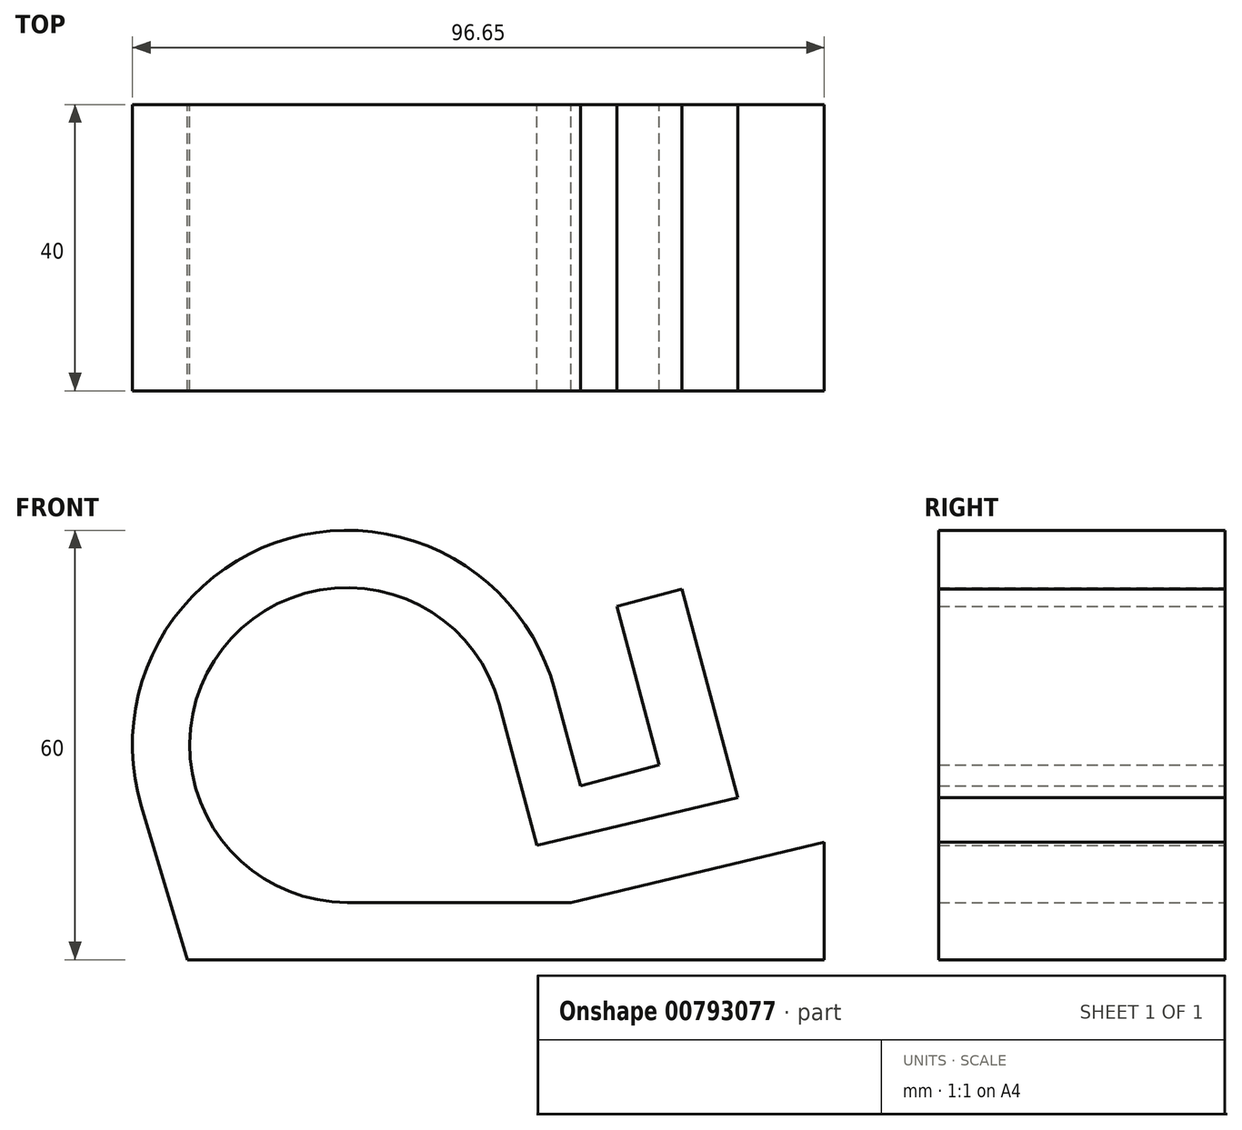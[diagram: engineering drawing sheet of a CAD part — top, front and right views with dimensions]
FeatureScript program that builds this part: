
annotation { "Feature Type Name" : "Feature", "Feature Type Description" : "" }
export const myFeature = defineFeature(function(context is Context, id is Id, definition is map)
    precondition{}
    {
        {
            var Q0;
            Q0=qCreatedBy(makeId("Front.planeOp"),FACE);
            var sketch = newSketch(context, id + "F0", { "sketchPlane" : qUnion([Q0])});
            skArc(sketch, "E0", {"start": v(7.58, 35.12) * mm, "mid": v(-29.6, 56.2) * mm, "end": v(-50.12, 18.71) * mm});
            skArc(sketch, "E1", {"start": v(-0.14, 33.04) * mm, "mid": v(-38.85, 40.74) * mm, "end": v(-21.4, 5.35) * mm});
            skLineSegment(sketch, "E2", {"start": v(-50.12, 18.71) * mm, "end": v(-43.7, -2.65) * mm});
            skLineSegment(sketch, "E3", {"start": v(-43.7, -2.65) * mm, "end": v(45.26, -2.65) * mm});
            skLineSegment(sketch, "E4", {"start": v(-21.4, 27.35) * mm, "end": v(62.99, 49.96) * mm, "construction": true});
            skLineSegment(sketch, "E5", {"start": v(-21.4, 27.35) * mm, "end": v(69, 27.35) * mm, "construction": true});
            skLineSegment(sketch, "E6.trimOffspring", {"start": v(-0.14, 33.04) * mm, "end": v(5.14, 13.34) * mm});
            skLineSegment(sketch, "E7", {"start": v(-1.13, 67.63) * mm, "end": v(11.2, 21.63) * mm});
            skLineSegment(sketch, "E8", {"start": v(-21.4, 5.35) * mm, "end": v(9.89, 5.35) * mm});
            skPoint(sketch, "E9.orphan", {"position": v(8.71, 0) * mm});
            skLineSegment(sketch, "E10.trimOffspring", {"start": v(17.7, -2.65) * mm, "end": v(17.76, -2.85) * mm});
            skLineSegment(sketch, "E11", {"start": v(33.2, 20.01) * mm, "end": v(5.14, 13.34) * mm});
            skLineSegment(sketch, "E12", {"start": v(33.2, 20.01) * mm, "end": v(25.38, 49.16) * mm});
            skLineSegment(sketch, "E13", {"start": v(25.38, 49.16) * mm, "end": v(16.28, 46.72) * mm});
            skLineSegment(sketch, "E14", {"start": v(16.28, 46.72) * mm, "end": v(22.21, 24.59) * mm});
            skLineSegment(sketch, "E15", {"start": v(22.21, 24.59) * mm, "end": v(11.2, 21.63) * mm});
            skLineSegment(sketch, "E16", {"start": v(45.26, -2.65) * mm, "end": v(45.26, 13.76) * mm});
            skLineSegment(sketch, "E17", {"start": v(45.26, 13.76) * mm, "end": v(9.89, 5.35) * mm});
            skSolve(sketch);
        }
        {
            var Q0;
            {var subQ1=sQuery(id+"F0.wireOp",EDGE,"E0");Q0=makeQuery(id+"F0.imprint","IMPRINT",FACE,{"disambiguationData":[TD([[makeQuery(id+"F0.imprint","IMPRINT",EDGE,{"derivedFrom":subQ1}),1.0]])]});}
            extrude(context, id + "F1", {"entities" : qUnion([Q0]), "depth" : 40 * mm, "offsetDistance" : 25 * mm});
        }
    });
